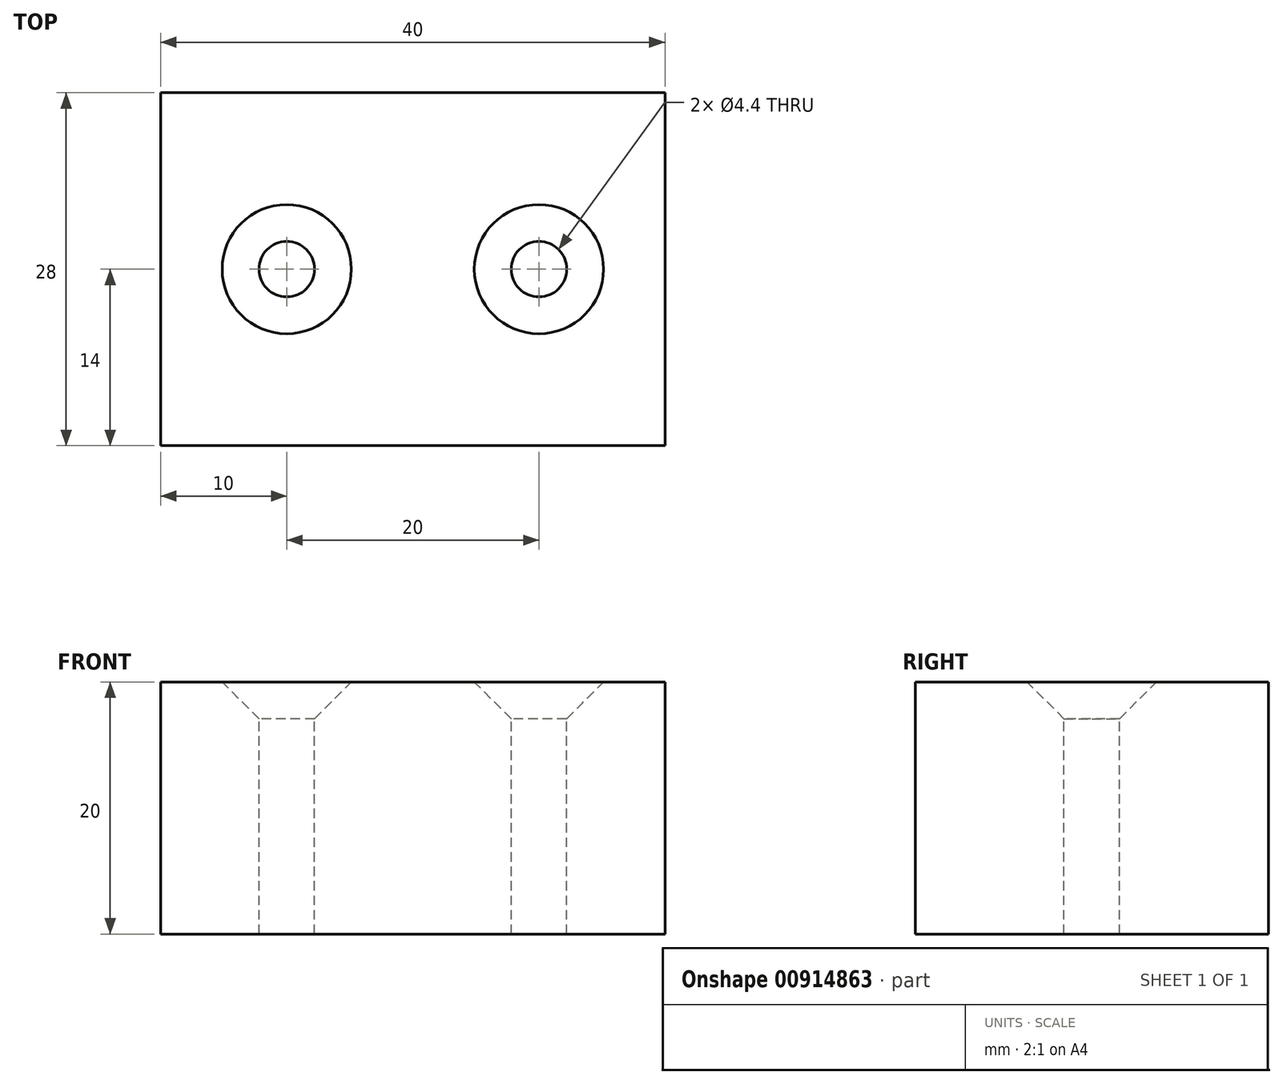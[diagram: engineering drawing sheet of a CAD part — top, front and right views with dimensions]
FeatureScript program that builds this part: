
annotation { "Feature Type Name" : "Feature", "Feature Type Description" : "" }
export const myFeature = defineFeature(function(context is Context, id is Id, definition is map)
    precondition{}
    {
        {
            var Q0;
            Q0=qCreatedBy(makeId("Top.planeOp"),FACE);
            var sketch = newSketch(context, id + "F0", { "sketchPlane" : qUnion([Q0])});
            skLineSegment(sketch, "E0.bottom", {"start": v(-25.36, 28.32) * mm, "end": v(14.64, 28.32) * mm});
            skLineSegment(sketch, "E0.top", {"start": v(-25.36, 0.32) * mm, "end": v(14.64, 0.32) * mm});
            skLineSegment(sketch, "E0.left", {"start": v(-25.36, 28.32) * mm, "end": v(-25.36, 0.32) * mm});
            skLineSegment(sketch, "E0.right", {"start": v(14.64, 28.32) * mm, "end": v(14.64, 0.32) * mm});
            skLineSegment(sketch, "E1", {"start": v(-25.36, 14.32) * mm, "end": v(14.64, 14.32) * mm, "construction": true});
            skCircle(sketch, "E2", {"center": v(-15.36, 14.32) * mm, "radius": 2.2 * mm});
            skCircle(sketch, "E3", {"center": v(4.64, 14.32) * mm, "radius": 2.2 * mm});
            skSolve(sketch);
        }
        {
            var Q0;
            Q0=makeQuery(id+"F0.imprint","IMPRINT",FACE,{"disambiguationData":[TD([[makeQuery(id+"F0.imprint","IMPRINT",EDGE,{"derivedFrom":sQuery(id+"F0.wireOp",EDGE,"E0.bottom")}),-1.0]])]});
            var Q1;
            Q1=makeQuery(id+"F0.imprint","IMPRINT",FACE,{"disambiguationData":[TD([[makeQuery(id+"F0.imprint","IMPRINT",EDGE,{"derivedFrom":sQuery(id+"F0.wireOp",EDGE,"E2")}),1.0]])]});
            var Q2;
            Q2=makeQuery(id+"F0.imprint","IMPRINT",FACE,{"disambiguationData":[TD([[makeQuery(id+"F0.imprint","IMPRINT",EDGE,{"derivedFrom":sQuery(id+"F0.wireOp",EDGE,"E3")}),1.0]])]});
            extrude(context, id + "F1", {"entities" : qUnion([Q0, Q1, Q2]), "oppositeDirection" : true, "depth" : 20 * mm, "offsetDistance" : 25 * mm});
        }
        {
            var Q0;
            Q0=sQuery(id+"F0.wireOp",VERTEX,"E3.center");
            var Q1;
            Q1=sQuery(id+"F0.wireOp",VERTEX,"E2.center");
            var Q2;
            Q2=makeQuery(id+"F1.opExtrude","SWEPT_BODY",BODY,{"disambiguationData":[OSD([sQuery(id+"F0.wireOp",EDGE,"E0.bottom"),sQuery(id+"F0.wireOp",EDGE,"E0.top"),sQuery(id+"F0.wireOp",EDGE,"E0.left"),sQuery(id+"F0.wireOp",EDGE,"E0.right")])]});
            hole(context, id + "F2", {"style" : HoleStyle.C_SINK, "endStyle" : HoleEndStyle.THROUGH, "holeDiameter" : 4.4 * mm, "cSinkDiameter" : 10.25 * mm, "cSinkAngle" : 90 * degree, "majorDiameter" : 5 * mm, "isTappedThrough" : true, "tappedDepth" : 12 * mm, "tapClearance" : 3, "locations" : qUnion([Q0, Q1]), "scope" : qUnion([Q2])});
        }
    });
